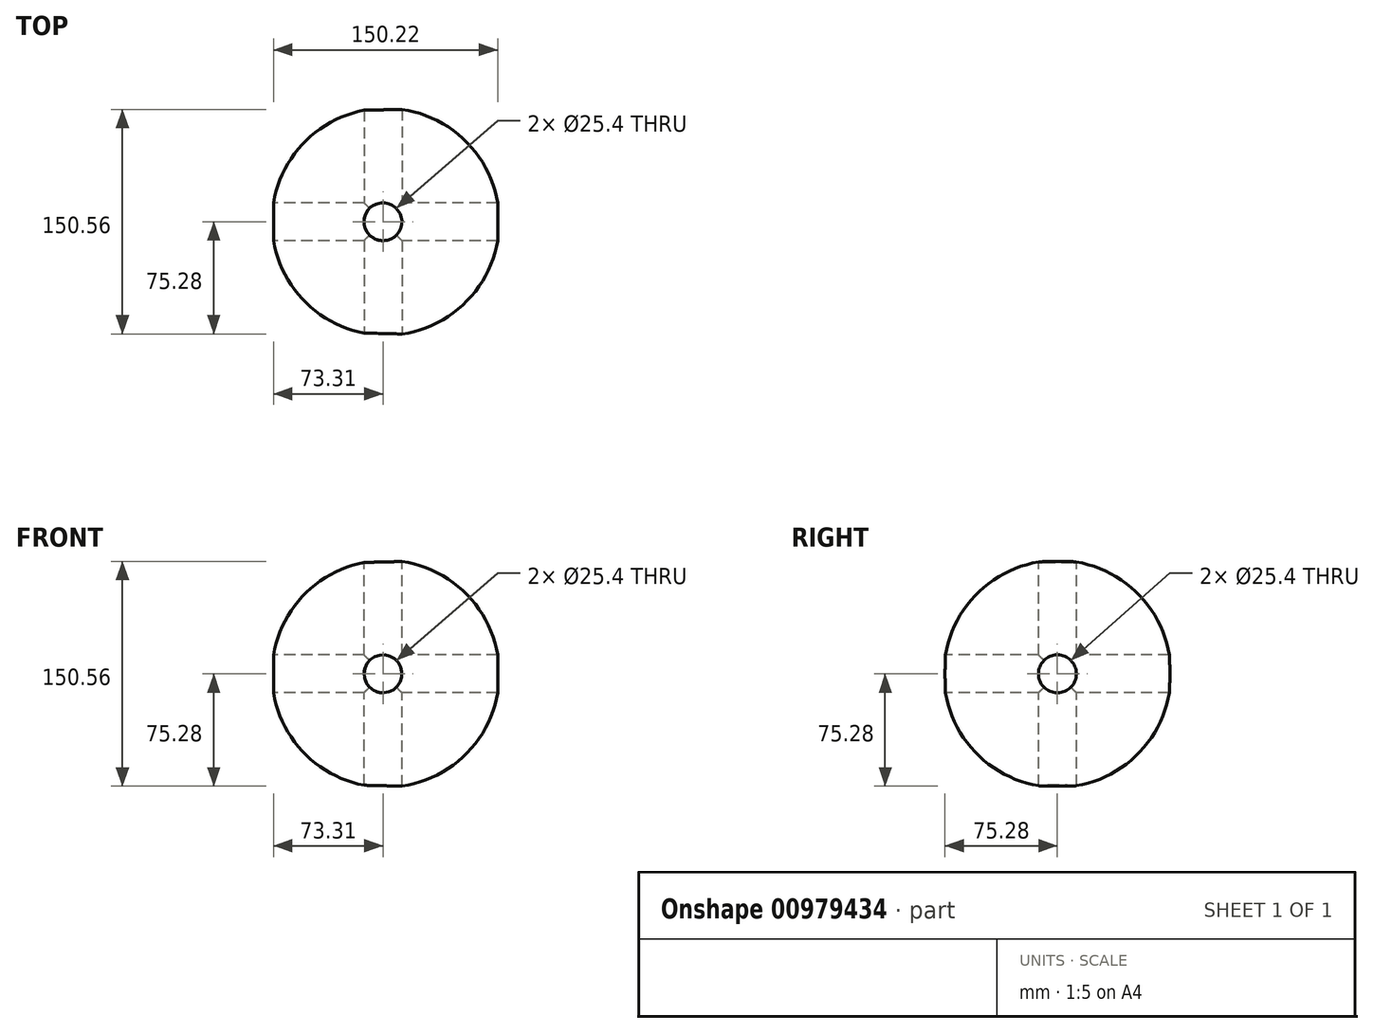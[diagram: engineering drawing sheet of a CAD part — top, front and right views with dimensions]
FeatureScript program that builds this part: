
annotation { "Feature Type Name" : "Feature", "Feature Type Description" : "" }
export const myFeature = defineFeature(function(context is Context, id is Id, definition is map)
    precondition{}
    {
        {
            var Q0;
            Q0=qCreatedBy(makeId("Top.planeOp"),FACE);
            var sketch = newSketch(context, id + "F0", { "sketchPlane" : qUnion([Q0])});
            skCircle(sketch, "E0", {"center": v(1.8, 0) * mm, "radius": 76.2 * mm, "construction": true});
            skArc(sketch, "E1", {"start": v(78, 0) * mm, "mid": v(1.8, 76.06) * mm, "end": v(-74.4, 0) * mm});
            skLineSegment(sketch, "E2", {"start": v(-74.4, 0) * mm, "end": v(78, 0) * mm});
            skSolve(sketch);
        }
        {
            var Q0;
            Q0 = qSketchRegion(id + "F0", true);
            var Q1;
            Q1=sQuery(id+"F0.wireOp",EDGE,"E2");
            revolve(context, id + "F1", {"surfaceOperationType" : NewSurfaceOperationType.NEW, "entities" : qUnion([Q0]), "axis" : qUnion([Q1]), "revolveType" : RevolveType.FULL});
        }
        {
            var Q0;
            Q0=qCreatedBy(makeId("Top.planeOp"),FACE);
            var sketch = newSketch(context, id + "F2", { "sketchPlane" : qUnion([Q0])});
            skCircle(sketch, "E3", {"center": v(0, 0) * mm, "radius": 12.7 * mm});
            skSolve(sketch);
        }
        {
            var Q0;
            Q0 = qSketchRegion(id + "F2", true);
            extrude(context, id + "F3", {"entities" : qUnion([Q0]), "operationType" : NewBodyOperationType.REMOVE, "endBound" : BoundingType.SYMMETRIC, "oppositeDirection" : true, "depth" : 177.8 * mm, "offsetDistance" : 25.4 * mm});
        }
        {
            var Q0;
            Q0=qCreatedBy(makeId("Right.planeOp"),FACE);
            var sketch = newSketch(context, id + "F4", { "sketchPlane" : qUnion([Q0])});
            skCircle(sketch, "E4", {"center": v(0, 0) * mm, "radius": 12.7 * mm});
            skSolve(sketch);
        }
        {
            var Q0;
            Q0 = qSketchRegion(id + "F4", true);
            extrude(context, id + "F5", {"entities" : qUnion([Q0]), "operationType" : NewBodyOperationType.REMOVE, "endBound" : BoundingType.SYMMETRIC, "depth" : 177.8 * mm, "offsetDistance" : 25.4 * mm});
        }
        {
            var Q0;
            Q0=qCreatedBy(makeId("Front.planeOp"),FACE);
            var sketch = newSketch(context, id + "F6", { "sketchPlane" : qUnion([Q0])});
            skCircle(sketch, "E5", {"center": v(0, 0) * mm, "radius": 12.7 * mm});
            skSolve(sketch);
        }
        {
            var Q0;
            Q0 = qSketchRegion(id + "F6", true);
            extrude(context, id + "F7", {"entities" : qUnion([Q0]), "operationType" : NewBodyOperationType.REMOVE, "endBound" : BoundingType.SYMMETRIC, "oppositeDirection" : true, "depth" : 177.8 * mm, "offsetDistance" : 25.4 * mm});
        }
    });
